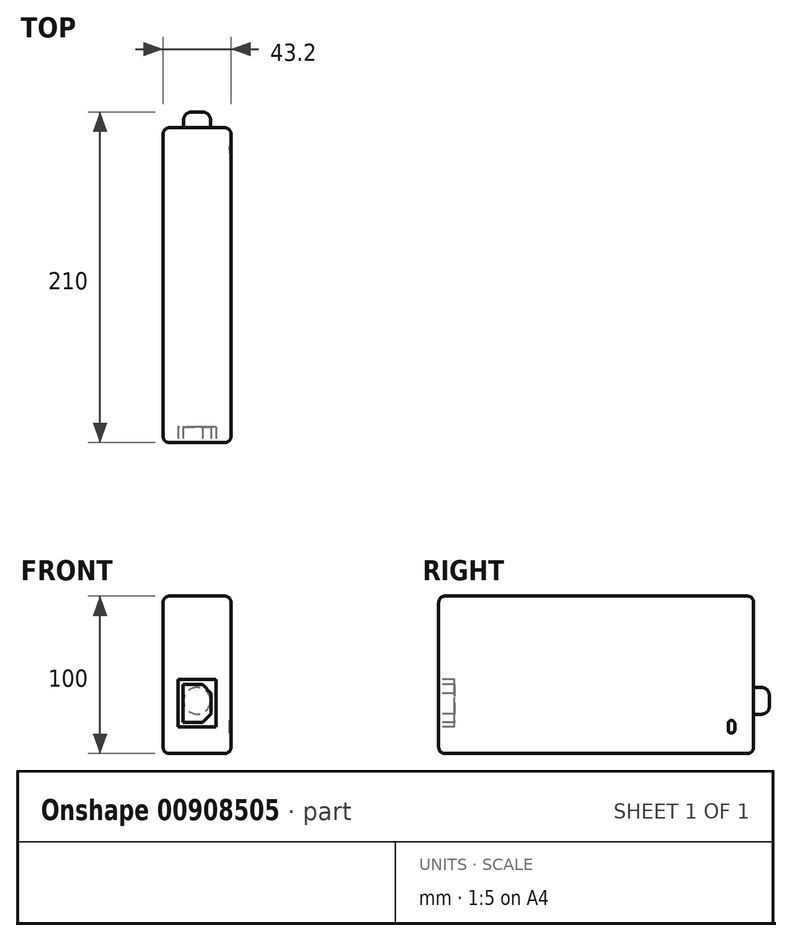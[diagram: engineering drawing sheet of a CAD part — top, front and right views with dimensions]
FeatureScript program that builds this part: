
annotation { "Feature Type Name" : "Feature", "Feature Type Description" : "" }
export const myFeature = defineFeature(function(context is Context, id is Id, definition is map)
    precondition{}
    {
        {
            var Q0;
            Q0=qCreatedBy(makeId("Right.planeOp"),FACE);
            var sketch = newSketch(context, id + "F0", { "sketchPlane" : qUnion([Q0])});
            skLineSegment(sketch, "E0.bottom", {"start": v(120.36, 60.38) * mm, "end": v(-79.64, 60.38) * mm});
            skLineSegment(sketch, "E0.top", {"start": v(120.36, -39.62) * mm, "end": v(-79.64, -39.62) * mm});
            skLineSegment(sketch, "E0.left", {"start": v(120.36, 60.38) * mm, "end": v(120.36, -39.62) * mm});
            skLineSegment(sketch, "E0.right", {"start": v(-79.64, 60.38) * mm, "end": v(-79.64, -39.62) * mm});
            skSolve(sketch);
        }
        {
            var Q0;
            Q0=makeQuery(id+"F0.imprint","IMPRINT",FACE,{"disambiguationData":[TD([[makeQuery(id+"F0.imprint","IMPRINT",EDGE,{"derivedFrom":sQuery(id+"F0.wireOp",EDGE,"E0.bottom")}),1.0]])]});
            extrude(context, id + "F1", {"entities" : qUnion([Q0]), "endBound" : BoundingType.SYMMETRIC, "depth" : 43.2 * mm, "offsetDistance" : 25 * mm});
        }
        {
            var Q0;
            Q0=makeQuery(id+"F1.opExtrude","SWEPT_EDGE",EDGE,{"disambiguationData":[OSD([sQuery(id+"F0.wireOp",EDGE,"E0.bottom"),sQuery(id+"F0.wireOp",EDGE,"E0.right")])]});
            var Q1;
            Q1=makeQuery(id+"F1.opExtrude","CAP_EDGE",EDGE,{"disambiguationData":[OSD([sQuery(id+"F0.wireOp",EDGE,"E0.right")])],"isStart":true});
            var Q2;
            Q2=makeQuery(id+"F1.opExtrude","CAP_EDGE",EDGE,{"disambiguationData":[OSD([sQuery(id+"F0.wireOp",EDGE,"E0.bottom")])],"isStart":true});
            var Q3;
            Q3=makeQuery(id+"F1.opExtrude","CAP_EDGE",EDGE,{"disambiguationData":[OSD([sQuery(id+"F0.wireOp",EDGE,"E0.bottom")])],"isStart":false});
            var Q4;
            Q4=makeQuery(id+"F1.opExtrude","CAP_EDGE",EDGE,{"disambiguationData":[OSD([sQuery(id+"F0.wireOp",EDGE,"E0.right")])],"isStart":false});
            var Q5;
            Q5=makeQuery(id+"F1.opExtrude","SWEPT_EDGE",EDGE,{"disambiguationData":[OSD([sQuery(id+"F0.wireOp",EDGE,"E0.top"),sQuery(id+"F0.wireOp",EDGE,"E0.right")])]});
            var Q6;
            Q6=makeQuery(id+"F1.opExtrude","CAP_EDGE",EDGE,{"disambiguationData":[OSD([sQuery(id+"F0.wireOp",EDGE,"E0.top")])],"isStart":true});
            var Q7;
            Q7=makeQuery(id+"F1.opExtrude","CAP_EDGE",EDGE,{"disambiguationData":[OSD([sQuery(id+"F0.wireOp",EDGE,"E0.top")])],"isStart":false});
            var Q8;
            Q8=makeQuery(id+"F1.opExtrude","CAP_EDGE",EDGE,{"disambiguationData":[OSD([sQuery(id+"F0.wireOp",EDGE,"E0.left")])],"isStart":false});
            var Q9;
            Q9=makeQuery(id+"F1.opExtrude","SWEPT_EDGE",EDGE,{"disambiguationData":[OSD([sQuery(id+"F0.wireOp",EDGE,"E0.top"),sQuery(id+"F0.wireOp",EDGE,"E0.left")])]});
            var Q10;
            Q10=makeQuery(id+"F1.opExtrude","CAP_EDGE",EDGE,{"disambiguationData":[OSD([sQuery(id+"F0.wireOp",EDGE,"E0.left")])],"isStart":true});
            var Q11;
            Q11=makeQuery(id+"F1.opExtrude","SWEPT_EDGE",EDGE,{"disambiguationData":[OSD([sQuery(id+"F0.wireOp",EDGE,"E0.bottom"),sQuery(id+"F0.wireOp",EDGE,"E0.left")])]});
            fillet(context, id + "F2", {"entities" : qUnion([Q0, Q1, Q2, Q3, Q4, Q5, Q6, Q7, Q8, Q9, Q10, Q11]), "radius" : 4 * mm, "tangentPropagation" : true, "allowEdgeOverflow" : false});
        }
        {
            var Q0;
            Q0=makeQuery(id+"F1.opExtrude","CAP_FACE",FACE,{"disambiguationData":[OSD([sQuery(id+"F0.wireOp",EDGE,"E0.bottom"),sQuery(id+"F0.wireOp",EDGE,"E0.top"),sQuery(id+"F0.wireOp",EDGE,"E0.left"),sQuery(id+"F0.wireOp",EDGE,"E0.right")])],"isStart":false});
            var sketch = newSketch(context, id + "F3", { "sketchPlane" : qUnion([Q0])});
            skLineSegment(sketch, "E1.bottom", {"start": v(106.36, -26.62) * mm, "end": v(106.26, -26.62) * mm});
            skLineSegment(sketch, "E1.top", {"start": v(106.36, -18.62) * mm, "end": v(106.26, -18.62) * mm});
            skLineSegment(sketch, "E1.left", {"start": v(108.36, -24.62) * mm, "end": v(108.36, -20.62) * mm});
            skLineSegment(sketch, "E1.right", {"start": v(104.26, -24.62) * mm, "end": v(104.26, -20.62) * mm});
            skPoint(sketch, "E2.visualSharp", {"position": v(108.36, -26.62) * mm});
            skArc(sketch, "E2.filletArc", {"start": v(106.36, -26.62) * mm, "mid": v(107.78, -26.04) * mm, "end": v(108.36, -24.62) * mm});
            skPoint(sketch, "E3.visualSharp", {"position": v(104.26, -26.62) * mm});
            skArc(sketch, "E3.filletArc", {"start": v(104.26, -24.62) * mm, "mid": v(104.85, -26.04) * mm, "end": v(106.26, -26.62) * mm});
            skPoint(sketch, "E4.visualSharp", {"position": v(108.36, -18.62) * mm});
            skArc(sketch, "E4.filletArc", {"start": v(108.36, -20.62) * mm, "mid": v(107.78, -19.2) * mm, "end": v(106.36, -18.62) * mm});
            skPoint(sketch, "E5.visualSharp", {"position": v(104.26, -18.62) * mm});
            skArc(sketch, "E5.filletArc", {"start": v(106.26, -18.62) * mm, "mid": v(104.85, -19.2) * mm, "end": v(104.26, -20.62) * mm});
            skSolve(sketch);
        }
        {
            var Q0;
            Q0=makeQuery(id+"F3.imprint","IMPRINT",FACE,{"disambiguationData":[TD([[makeQuery(id+"F3.imprint","IMPRINT",EDGE,{"derivedFrom":sQuery(id+"F3.wireOp",EDGE,"E1.bottom")}),-1.0]])]});
            extrude(context, id + "F4", {"entities" : qUnion([Q0]), "operationType" : NewBodyOperationType.REMOVE, "oppositeDirection" : true, "depth" : 1 * mm, "offsetDistance" : 25 * mm});
        }
        {
            var Q0;
            Q0=makeQuery(id+"F1.opExtrude","SWEPT_FACE",FACE,{"disambiguationData":[OSD([sQuery(id+"F0.wireOp",EDGE,"E0.left")])]});
            var sketch = newSketch(context, id + "F5", { "sketchPlane" : qUnion([Q0])});
            skCircle(sketch, "E6", {"center": v(0, -6.12) * mm, "radius": 8.5 * mm});
            skSolve(sketch);
        }
        {
            var Q0;
            Q0=makeQuery(id+"F5.imprint","IMPRINT",FACE,{"disambiguationData":[TD([[makeQuery(id+"F5.imprint","IMPRINT",EDGE,{"derivedFrom":sQuery(id+"F5.wireOp",EDGE,"E6")}),1.0]])]});
            extrude(context, id + "F6", {"entities" : qUnion([Q0]), "operationType" : NewBodyOperationType.ADD, "depth" : 10 * mm, "offsetDistance" : 25 * mm});
        }
        {
            var Q0;
            Q0=makeQuery(id+"F6.opExtrude","CAP_EDGE",EDGE,{"disambiguationData":[OSD([sQuery(id+"F5.wireOp",EDGE,"E6")])],"isStart":false});
            fillet(context, id + "F7", {"entities" : qUnion([Q0]), "radius" : 5 * mm, "tangentPropagation" : true, "allowEdgeOverflow" : false});
        }
        {
            var Q0;
            Q0=makeQuery(id+"F1.opExtrude","SWEPT_FACE",FACE,{"disambiguationData":[OSD([sQuery(id+"F0.wireOp",EDGE,"E0.right")])]});
            var sketch = newSketch(context, id + "F8", { "sketchPlane" : qUnion([Q0])});
            skLineSegment(sketch, "E7.bottom", {"start": v(12, -22.82) * mm, "end": v(-12, -22.82) * mm});
            skLineSegment(sketch, "E7.top", {"start": v(12, 7.58) * mm, "end": v(-12, 7.58) * mm});
            skLineSegment(sketch, "E7.left", {"start": v(12, -22.82) * mm, "end": v(12, 7.58) * mm});
            skLineSegment(sketch, "E7.right", {"start": v(-12, -22.82) * mm, "end": v(-12, 7.58) * mm});
            skLineSegment(sketch, "E8", {"start": v(-9, 4.18) * mm, "end": v(-9, -19.82) * mm});
            skLineSegment(sketch, "E9", {"start": v(-9, -19.82) * mm, "end": v(3.58, -19.82) * mm});
            skLineSegment(sketch, "E10", {"start": v(3.58, -19.82) * mm, "end": v(9, -14.32) * mm});
            skLineSegment(sketch, "E11", {"start": v(9, -14.32) * mm, "end": v(9, -1.32) * mm});
            skLineSegment(sketch, "E12", {"start": v(9, -1.32) * mm, "end": v(3.58, 4.39) * mm});
            skLineSegment(sketch, "E13", {"start": v(3.58, 4.39) * mm, "end": v(-9, 4.18) * mm});
            skLineSegment(sketch, "E14", {"start": v(9, -7.82) * mm, "end": v(-9, -7.82) * mm, "construction": true});
            skPoint(sketch, "E14.endSnap0", {"position": v(-9, -7.82) * mm});
            skSolve(sketch);
        }
        {
            var Q0;
            Q0=makeQuery(id+"F8.imprint","IMPRINT",FACE,{"disambiguationData":[TD([[makeQuery(id+"F8.imprint","IMPRINT",EDGE,{"derivedFrom":sQuery(id+"F8.wireOp",EDGE,"E7.bottom")}),-1.0]])]});
            extrude(context, id + "F9", {"entities" : qUnion([Q0]), "operationType" : NewBodyOperationType.REMOVE, "oppositeDirection" : true, "depth" : 10 * mm, "offsetDistance" : 25 * mm});
        }
    });
